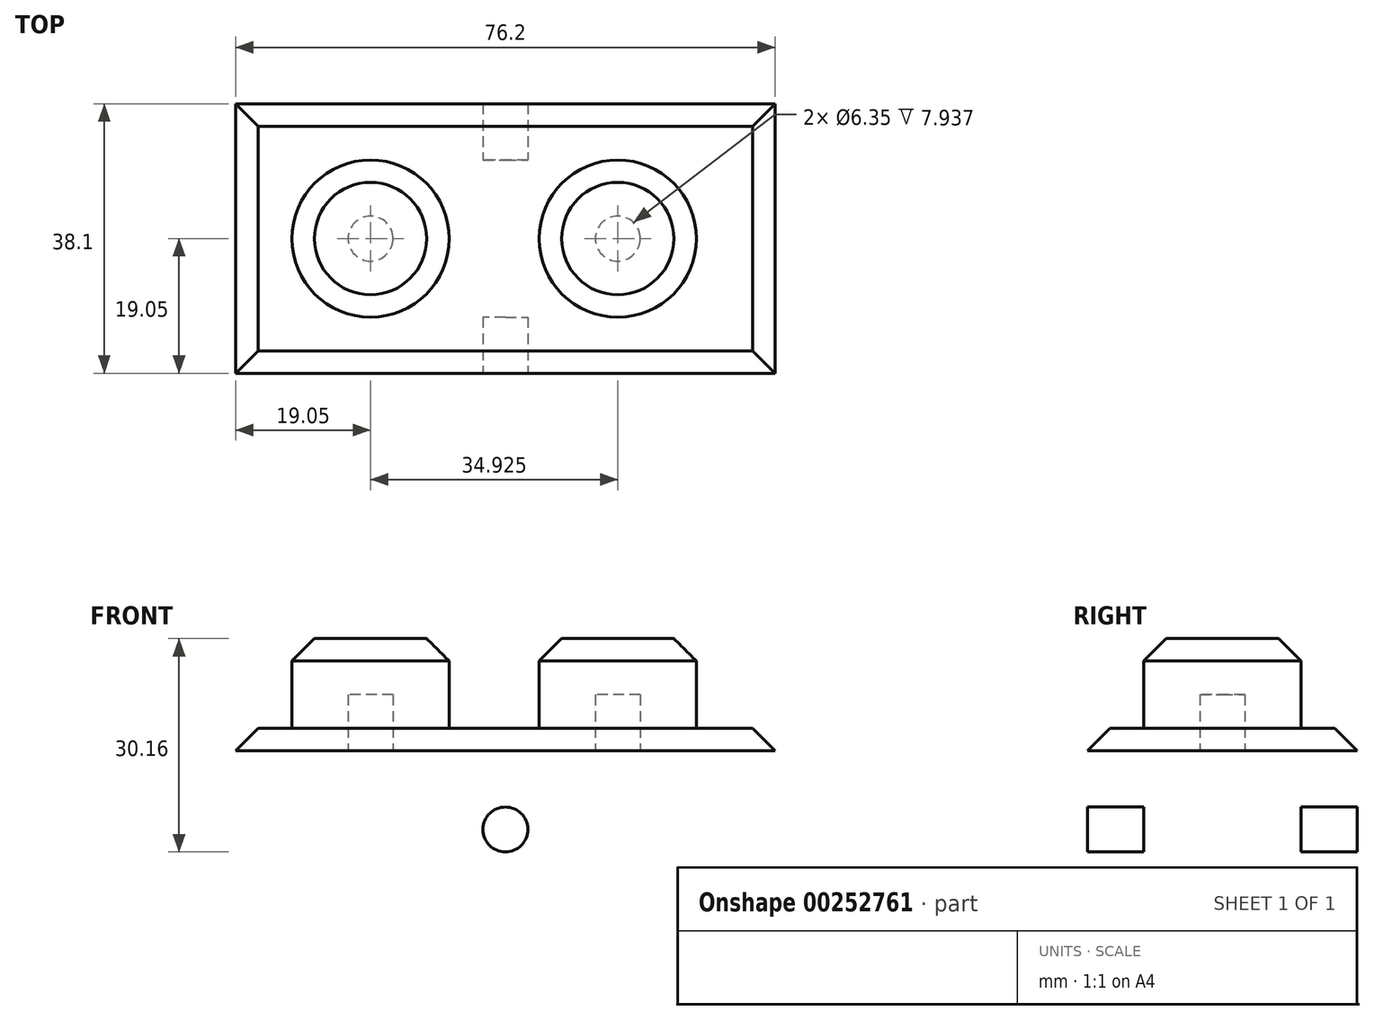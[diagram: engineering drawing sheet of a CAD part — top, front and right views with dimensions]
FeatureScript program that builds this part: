
annotation { "Feature Type Name" : "Feature", "Feature Type Description" : "" }
export const myFeature = defineFeature(function(context is Context, id is Id, definition is map)
    precondition{}
    {
        {
            var Q0;
            Q0=qCreatedBy(makeId("Top.planeOp"),FACE);
            var sketch = newSketch(context, id + "F0", { "sketchPlane" : qUnion([Q0])});
            skLineSegment(sketch, "E0.bottom", {"start": v(0, 0) * mm, "end": v(76.2, 0) * mm});
            skLineSegment(sketch, "E0.top", {"start": v(0, -38.1) * mm, "end": v(76.2, -38.1) * mm});
            skLineSegment(sketch, "E0.left", {"start": v(0, 0) * mm, "end": v(0, -38.1) * mm});
            skLineSegment(sketch, "E0.right", {"start": v(76.2, 0) * mm, "end": v(76.2, -38.1) * mm});
            skSolve(sketch);
        }
        {
            var Q0;
            Q0 = qSketchRegion(id + "F0", true);
            extrude(context, id + "F1", {"entities" : qUnion([Q0]), "depth" : 25.4 * mm});
        }
        {
            var Q0;
            Q0=makeQuery(id+"F1.opExtrude","CAP_FACE",FACE,{"disambiguationData":[OSD([sQuery(id+"F0.wireOp",EDGE,"E0.bottom"),sQuery(id+"F0.wireOp",EDGE,"E0.top"),sQuery(id+"F0.wireOp",EDGE,"E0.left"),sQuery(id+"F0.wireOp",EDGE,"E0.right")])],"isStart":false});
            var sketch = newSketch(context, id + "F2", { "sketchPlane" : qUnion([Q0])});
            skLineSegment(sketch, "E1", {"start": v(0, -19.05) * mm, "end": v(19.05, -19.05) * mm});
            skPoint(sketch, "E1.endSnap0", {"position": v(0, -19.05) * mm});
            skCircle(sketch, "E2", {"center": v(19.05, -19.05) * mm, "radius": 11.11 * mm});
            skLineSegment(sketch, "E3", {"start": v(76.2, -19.05) * mm, "end": v(53.98, -19.05) * mm});
            skPoint(sketch, "E3.endSnap0", {"position": v(76.2, -19.05) * mm});
            skCircle(sketch, "E4", {"center": v(53.98, -19.05) * mm, "radius": 11.11 * mm});
            skSolve(sketch);
        }
        {
            var Q0;
            Q0 = qSketchRegion(id + "F2", true);
            extrude(context, id + "F3", {"entities" : qUnion([Q0]), "operationType" : NewBodyOperationType.ADD, "depth" : 12.7 * mm});
        }
        {
            var Q0;
            Q0=makeQuery(id+"F1.opExtrude","CAP_FACE",FACE,{"disambiguationData":[OSD([sQuery(id+"F0.wireOp",EDGE,"E0.bottom"),sQuery(id+"F0.wireOp",EDGE,"E0.top"),sQuery(id+"F0.wireOp",EDGE,"E0.left"),sQuery(id+"F0.wireOp",EDGE,"E0.right")])],"isStart":true});
            shell(context, id + "F4", {"entities" : qUnion([Q0]), "thickness" : 7.94 * mm});
        }
        {
            var Q0;
            Q0=makeQuery(id+"F1.opExtrude","CAP_EDGE",EDGE,{"disambiguationData":[OSD([sQuery(id+"F0.wireOp",EDGE,"E0.top")])],"isStart":false});
            var Q1;
            Q1=makeQuery(id+"F1.opExtrude","CAP_EDGE",EDGE,{"disambiguationData":[OSD([sQuery(id+"F0.wireOp",EDGE,"E0.left")])],"isStart":false});
            var Q2;
            Q2=makeQuery(id+"F1.opExtrude","CAP_EDGE",EDGE,{"disambiguationData":[OSD([sQuery(id+"F0.wireOp",EDGE,"E0.bottom")])],"isStart":false});
            var Q3;
            Q3=makeQuery(id+"F1.opExtrude","CAP_EDGE",EDGE,{"disambiguationData":[OSD([sQuery(id+"F0.wireOp",EDGE,"E0.right")])],"isStart":false});
            var Q4;
            Q4=makeQuery(id+"F3.opExtrude","CAP_EDGE",EDGE,{"disambiguationData":[OSD([sQuery(id+"F2.wireOp",EDGE,"E4")])],"isStart":false});
            var Q5;
            Q5=makeQuery(id+"F3.opExtrude","CAP_EDGE",EDGE,{"disambiguationData":[OSD([sQuery(id+"F2.wireOp",EDGE,"E2")])],"isStart":false});
            chamfer(context, id + "F5", {"entities" : qUnion([Q0, Q1, Q2, Q3, Q4, Q5]), "chamferType" : ChamferType.OFFSET_ANGLE, "width" : 3.17 * mm, "oppositeDirection" : false, "angle" : 45 * degree, "tangentPropagation" : true});
        }
        {
            var Q0;
            Q0=makeQuery(id+"F1.opExtrude","SWEPT_FACE",FACE,{"disambiguationData":[OSD([sQuery(id+"F0.wireOp",EDGE,"E0.top")])]});
            var sketch = newSketch(context, id + "F6", { "sketchPlane" : qUnion([Q0])});
            skLineSegment(sketch, "E5", {"start": v(38.1, 22.23) * mm, "end": v(38.1, 0) * mm});
            skCircle(sketch, "E6", {"center": v(38.1, 11.11) * mm, "radius": 3.18 * mm});
            skSolve(sketch);
        }
        {
            var Q0;
            {var subQ0=sQuery(id+"F6.wireOp",EDGE,"E6");var subQ1=sQuery(id+"F6.wireOp",EDGE,"E5");var subQ2=makeQuery(id+"F6.imprint","INTERSECT",VERTEX,{"disambiguationData":[OD(0.0)],"derivedFrom":[subQ1,subQ0]});Q0=makeQuery(id+"F6.imprint","IMPRINT",FACE,{"disambiguationData":[TD([[makeQuery(id+"F6.imprint","IMPRINT",EDGE,{"disambiguationData":[TD([[subQ2,-1.0]])],"derivedFrom":subQ1}),1.0]])]});}
            var Q1;
            {var subQ0=sQuery(id+"F6.wireOp",EDGE,"E6");var subQ1=sQuery(id+"F6.wireOp",EDGE,"E5");var subQ2=makeQuery(id+"F6.imprint","INTERSECT",VERTEX,{"disambiguationData":[OD(0.0)],"derivedFrom":[subQ1,subQ0]});Q1=makeQuery(id+"F6.imprint","IMPRINT",FACE,{"disambiguationData":[TD([[makeQuery(id+"F6.imprint","IMPRINT",EDGE,{"disambiguationData":[TD([[subQ2,-1.0]])],"derivedFrom":subQ1}),-1.0]])]});}
            var Q2;
            Q2=sQuery(id+"F6.wireOp",EDGE,"E6");
            extrude(context, id + "F7", {"entities" : qUnion([Q0, Q1]), "operationType" : NewBodyOperationType.REMOVE, "surfaceEntities" : qUnion([Q2]), "endBound" : BoundingType.THROUGH_ALL, "oppositeDirection" : true, "depth" : 25.4 * mm});
        }
    });
